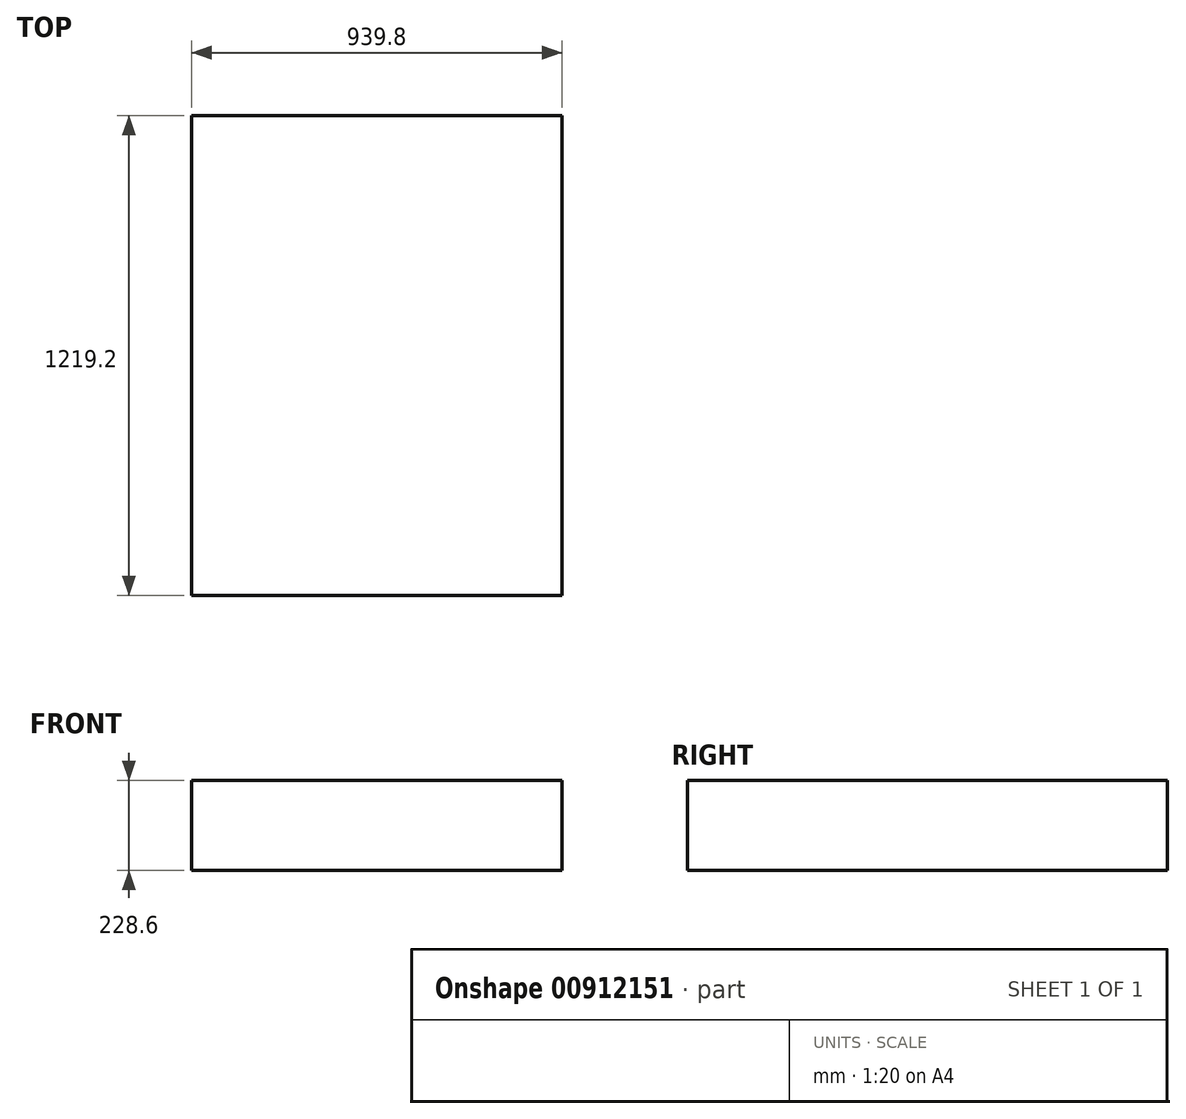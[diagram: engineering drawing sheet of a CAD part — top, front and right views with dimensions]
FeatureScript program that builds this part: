
annotation { "Feature Type Name" : "Feature", "Feature Type Description" : "" }
export const myFeature = defineFeature(function(context is Context, id is Id, definition is map)
    precondition{}
    {
        {
            var Q0;
            Q0=qCreatedBy(makeId("Front.planeOp"),FACE);
            var sketch = newSketch(context, id + "F0", { "sketchPlane" : qUnion([Q0])});
            skLineSegment(sketch, "E0.bottom", {"start": v(-853.31, 220.93) * mm, "end": v(86.49, 220.93) * mm});
            skLineSegment(sketch, "E0.top", {"start": v(-853.31, -7.67) * mm, "end": v(86.49, -7.67) * mm});
            skLineSegment(sketch, "E0.left", {"start": v(-853.31, 220.93) * mm, "end": v(-853.31, -7.67) * mm});
            skLineSegment(sketch, "E0.right", {"start": v(86.49, 220.93) * mm, "end": v(86.49, -7.67) * mm});
            skSolve(sketch);
        }
        {
            var Q0;
            Q0=makeQuery(id+"F0.imprint","IMPRINT",FACE,{"disambiguationData":[TD([[makeQuery(id+"F0.imprint","IMPRINT",EDGE,{"derivedFrom":sQuery(id+"F0.wireOp",EDGE,"E0.bottom")}),-1.0]])]});
            extrude(context, id + "F1", {"entities" : qUnion([Q0]), "oppositeDirection" : true, "depth" : 1219.2 * mm, "offsetDistance" : 25.4 * mm});
        }
    });
